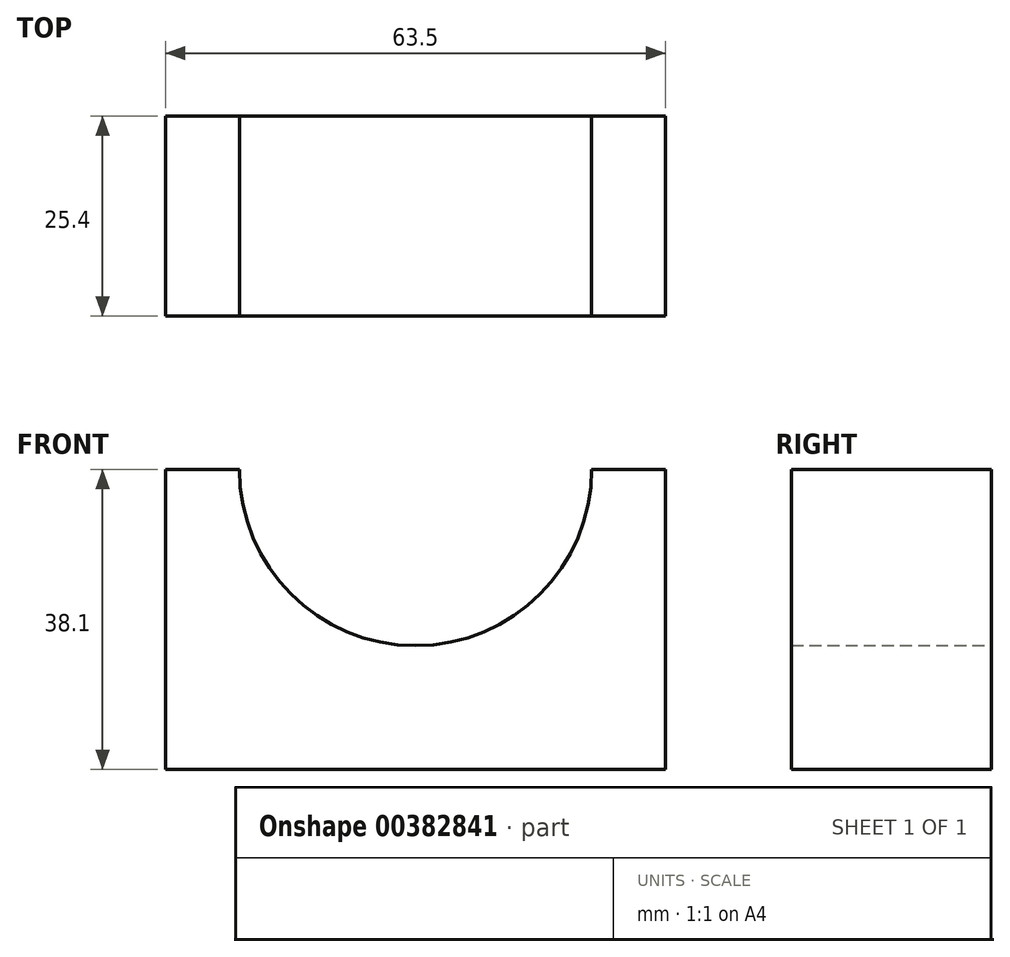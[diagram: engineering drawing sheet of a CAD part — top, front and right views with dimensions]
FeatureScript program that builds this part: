
annotation { "Feature Type Name" : "Feature", "Feature Type Description" : "" }
export const myFeature = defineFeature(function(context is Context, id is Id, definition is map)
    precondition{}
    {
        {
            var Q0;
            Q0=qCreatedBy(makeId("Front.planeOp"),FACE);
            var sketch = newSketch(context, id + "F0", { "sketchPlane" : qUnion([Q0])});
            skLineSegment(sketch, "E0", {"start": v(0, 0) * mm, "end": v(63.5, 0) * mm});
            skLineSegment(sketch, "E1", {"start": v(63.5, 0) * mm, "end": v(63.5, 38.1) * mm});
            skLineSegment(sketch, "E2", {"start": v(63.5, 38.1) * mm, "end": v(0, 38.1) * mm});
            skLineSegment(sketch, "E3", {"start": v(0, 38.1) * mm, "end": v(0, 0) * mm});
            skSolve(sketch);
        }
        {
            var Q0;
            Q0 = qSketchRegion(id + "F0", true);
            extrude(context, id + "F1", {"entities" : qUnion([Q0]), "depth" : 25.4 * mm});
        }
        {
            var Q0;
            Q0=qCreatedBy(makeId("Front.planeOp"),FACE);
            var sketch = newSketch(context, id + "F2", { "sketchPlane" : qUnion([Q0])});
            skCircle(sketch, "E4", {"center": v(31.75, 38.1) * mm, "radius": 22.37 * mm});
            skSolve(sketch);
        }
        {
            var Q0;
            Q0 = qSketchRegion(id + "F2", true);
            extrude(context, id + "F3", {"entities" : qUnion([Q0]), "operationType" : NewBodyOperationType.REMOVE, "depth" : 25.4 * mm});
        }
    });
